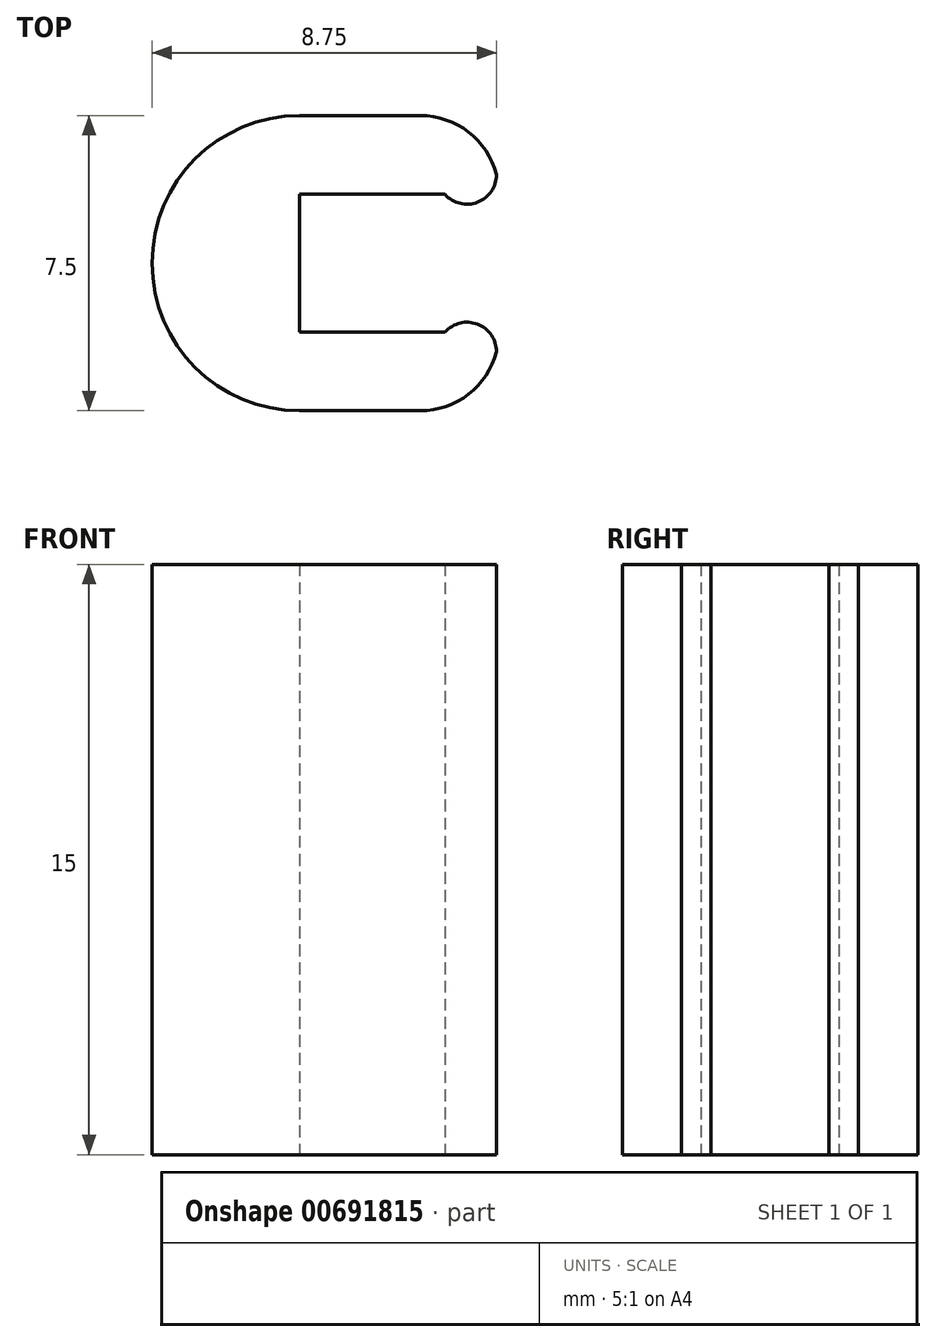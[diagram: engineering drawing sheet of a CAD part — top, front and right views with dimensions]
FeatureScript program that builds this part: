
annotation { "Feature Type Name" : "Feature", "Feature Type Description" : "" }
export const myFeature = defineFeature(function(context is Context, id is Id, definition is map)
    precondition{}
    {
        {
            var Q0;
            Q0=qCreatedBy(makeId("Top.planeOp"),FACE);
            var sketch = newSketch(context, id + "F0", { "sketchPlane" : qUnion([Q0])});
            skLineSegment(sketch, "E0", {"start": v(0, 1.64) * mm, "end": v(-5, 1.64) * mm});
            skLineSegment(sketch, "E1", {"start": v(-5, 1.64) * mm, "end": v(-5, -1.86) * mm});
            skLineSegment(sketch, "E2", {"start": v(-5, -1.86) * mm, "end": v(0, -1.86) * mm});
            skLineSegment(sketch, "E3", {"start": v(0, -1.86) * mm, "end": v(0, -3.86) * mm});
            skLineSegment(sketch, "E4", {"start": v(0, -3.86) * mm, "end": v(-10, -3.86) * mm});
            skLineSegment(sketch, "E5", {"start": v(-10, -3.86) * mm, "end": v(-10, 3.64) * mm});
            skLineSegment(sketch, "E6", {"start": v(-10, 3.64) * mm, "end": v(0, 3.64) * mm});
            skLineSegment(sketch, "E7", {"start": v(0, 3.64) * mm, "end": v(0, 1.64) * mm});
            skCircle(sketch, "E8", {"center": v(-0.75, 2.14) * mm, "radius": 0.75 * mm});
            skCircle(sketch, "E9", {"center": v(-0.75, -2.36) * mm, "radius": 0.75 * mm});
            skCircle(sketch, "E10", {"center": v(-5, -0.11) * mm, "radius": 3.75 * mm});
            skSolve(sketch);
        }
        {
            var Q0;
            {var subQ1=sQuery(id+"F0.wireOp",EDGE,"E1");Q0=makeQuery(id+"F0.imprint","IMPRINT",FACE,{"disambiguationData":[TD([[makeQuery(id+"F0.imprint","IMPRINT",EDGE,{"derivedFrom":subQ1}),-1.0]])]});}
            var Q1;
            {var subQ1=sQuery(id+"F0.wireOp",EDGE,"E2");var subQ7=sQuery(id+"F0.wireOp",EDGE,"E10");var subQ9=makeQuery(id+"F0.imprint","INTERSECT",VERTEX,{"derivedFrom":[subQ1,subQ7]});Q1=makeQuery(id+"F0.imprint","IMPRINT",FACE,{"disambiguationData":[TD([[makeQuery(id+"F0.imprint","IMPRINT",EDGE,{"disambiguationData":[TD([[subQ9,-1.0]])],"derivedFrom":subQ1}),-1.0]])]});}
            var Q2;
            {var subQ0=sQuery(id+"F0.wireOp",EDGE,"E9");var subQ1=sQuery(id+"F0.wireOp",EDGE,"E2");var subQ2=makeQuery(id+"F0.imprint","INTERSECT",VERTEX,{"disambiguationData":[OD(0.0)],"derivedFrom":[subQ1,subQ0]});Q2=makeQuery(id+"F0.imprint","IMPRINT",FACE,{"disambiguationData":[TD([[makeQuery(id+"F0.imprint","IMPRINT",EDGE,{"disambiguationData":[TD([[subQ2,-1.0]])],"derivedFrom":subQ1}),-1.0]])]});}
            var Q3;
            {var subQ0=sQuery(id+"F0.wireOp",EDGE,"E9");var subQ1=sQuery(id+"F0.wireOp",EDGE,"E2");var subQ2=makeQuery(id+"F0.imprint","INTERSECT",VERTEX,{"disambiguationData":[OD(0.0)],"derivedFrom":[subQ1,subQ0]});Q3=makeQuery(id+"F0.imprint","IMPRINT",FACE,{"disambiguationData":[TD([[makeQuery(id+"F0.imprint","IMPRINT",EDGE,{"disambiguationData":[TD([[subQ2,-1.0]])],"derivedFrom":subQ1}),1.0]])]});}
            var Q4;
            {var subQ0=sQuery(id+"F0.wireOp",EDGE,"E8");var subQ1=sQuery(id+"F0.wireOp",EDGE,"E0");var subQ2=makeQuery(id+"F0.imprint","INTERSECT",VERTEX,{"disambiguationData":[OD(0.0)],"derivedFrom":[subQ1,subQ0]});Q4=makeQuery(id+"F0.imprint","IMPRINT",FACE,{"disambiguationData":[TD([[makeQuery(id+"F0.imprint","IMPRINT",EDGE,{"disambiguationData":[TD([[subQ2,-1.0]])],"derivedFrom":subQ1}),1.0]])]});}
            var Q5;
            {var subQ0=sQuery(id+"F0.wireOp",EDGE,"E8");var subQ1=sQuery(id+"F0.wireOp",EDGE,"E0");var subQ2=makeQuery(id+"F0.imprint","INTERSECT",VERTEX,{"disambiguationData":[OD(0.0)],"derivedFrom":[subQ1,subQ0]});Q5=makeQuery(id+"F0.imprint","IMPRINT",FACE,{"disambiguationData":[TD([[makeQuery(id+"F0.imprint","IMPRINT",EDGE,{"disambiguationData":[TD([[subQ2,-1.0]])],"derivedFrom":subQ1}),-1.0]])]});}
            var Q6;
            {var subQ0=sQuery(id+"F0.wireOp",EDGE,"E8");var subQ1=sQuery(id+"F0.wireOp",EDGE,"E0");var subQ2=makeQuery(id+"F0.imprint","INTERSECT",VERTEX,{"disambiguationData":[OD(1.0)],"derivedFrom":[subQ1,subQ0]});Q6=makeQuery(id+"F0.imprint","IMPRINT",FACE,{"disambiguationData":[TD([[makeQuery(id+"F0.imprint","IMPRINT",EDGE,{"disambiguationData":[TD([[subQ2,-1.0]])],"derivedFrom":subQ1}),-1.0]])]});}
            extrude(context, id + "F1", {"entities" : qUnion([Q0, Q1, Q2, Q3, Q4, Q5, Q6]), "depth" : 15 * mm, "offsetDistance" : 25 * mm});
        }
        {
            var Q0;
            Q0=makeQuery(id+"F1.opExtrude","SWEPT_EDGE",EDGE,{"disambiguationData":[OSD([sQuery(id+"F0.wireOp",EDGE,"E6"),sQuery(id+"F0.wireOp",EDGE,"E7")])]});
            var Q1;
            Q1=makeQuery(id+"F1.opExtrude","SWEPT_EDGE",EDGE,{"disambiguationData":[OSD([sQuery(id+"F0.wireOp",EDGE,"E3"),sQuery(id+"F0.wireOp",EDGE,"E4")])]});
            fillet(context, id + "F2", {"entities" : qUnion([Q0, Q1]), "radius" : 2 * mm, "tangentPropagation" : true, "allowEdgeOverflow" : false});
        }
    });
